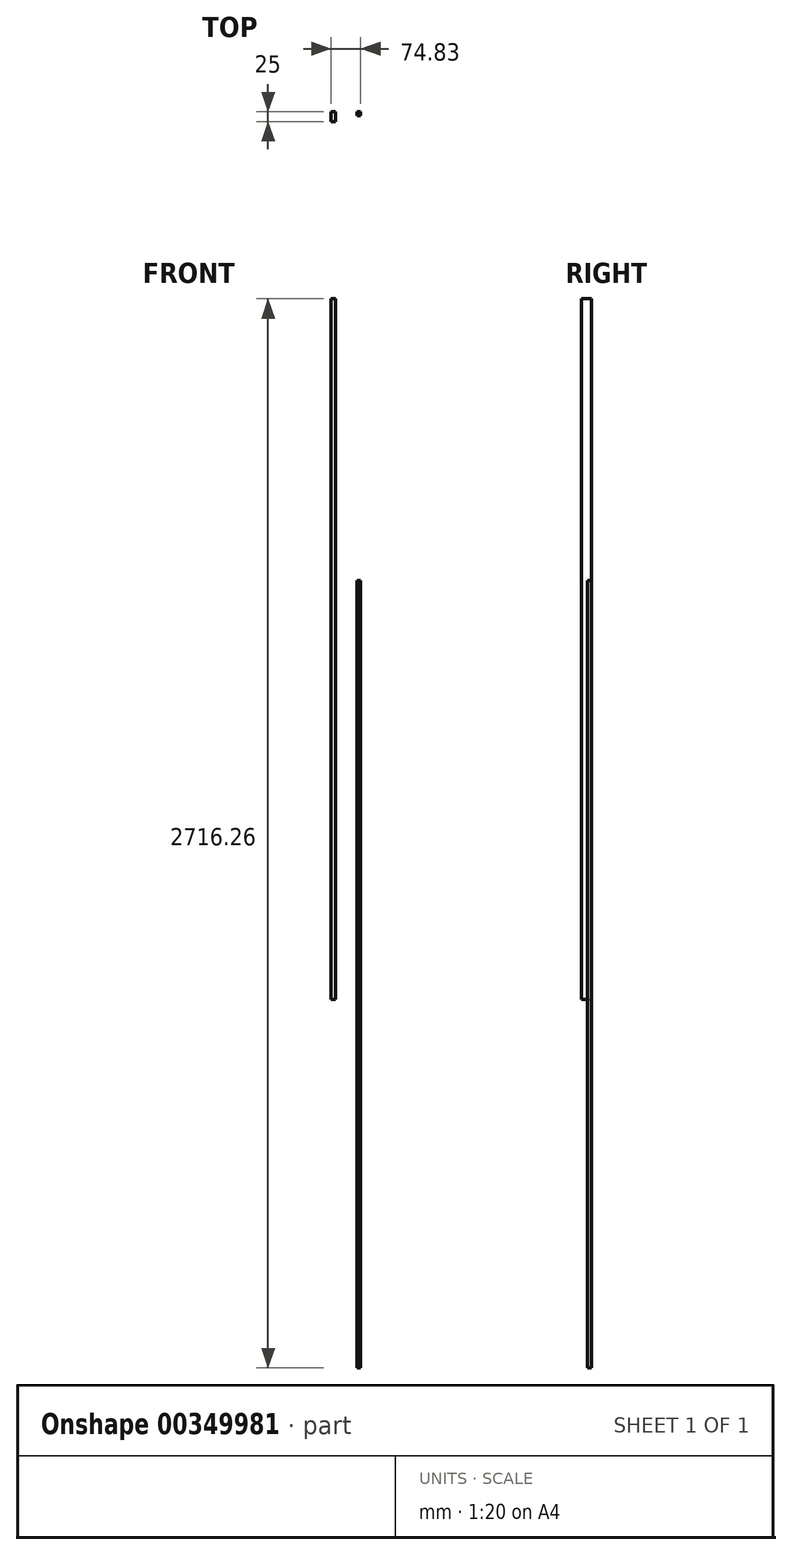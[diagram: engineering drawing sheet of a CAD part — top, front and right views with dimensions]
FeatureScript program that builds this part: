
annotation { "Feature Type Name" : "Feature", "Feature Type Description" : "" }
export const myFeature = defineFeature(function(context is Context, id is Id, definition is map)
    precondition{}
    {
        {
            var Q0;
            Q0=qCreatedBy(makeId("Front.planeOp"),FACE);
            var sketch = newSketch(context, id + "F0", { "sketchPlane" : qUnion([Q0])});
            skLineSegment(sketch, "E0.bottom", {"start": v(5, -1000) * mm, "end": v(-5, -1000) * mm});
            skLineSegment(sketch, "E0.top", {"start": v(5, 1000) * mm, "end": v(-5, 1000) * mm});
            skLineSegment(sketch, "E0.left", {"start": v(5, -1000) * mm, "end": v(5, 1000) * mm});
            skLineSegment(sketch, "E0.right", {"start": v(-5, -1000) * mm, "end": v(-5, 1000) * mm});
            skPoint(sketch, "E0.middle", {"position": v(0, 0) * mm});
            skSolve(sketch);
        }
        {
            var Q0;
            Q0 = qSketchRegion(id + "F0", true);
            extrude(context, id + "F1", {"entities" : qUnion([Q0]), "depth" : 10 * mm, "offsetDistance" : 25 * mm});
        }
        {
            var Q0;
            Q0=qCreatedBy(makeId("Front.planeOp"),FACE);
            var sketch = newSketch(context, id + "F2", { "sketchPlane" : qUnion([Q0])});
            skLineSegment(sketch, "E1.bottom", {"start": v(-69.83, 1716.26) * mm, "end": v(-58.97, 1716.26) * mm});
            skLineSegment(sketch, "E1.top", {"start": v(-69.83, -63.74) * mm, "end": v(-58.97, -63.74) * mm});
            skLineSegment(sketch, "E1.left", {"start": v(-69.83, 1716.26) * mm, "end": v(-69.83, -63.74) * mm});
            skLineSegment(sketch, "E1.right", {"start": v(-58.97, 1716.26) * mm, "end": v(-58.97, -63.74) * mm});
            skSolve(sketch);
        }
        {
            var Q0;
            Q0 = qSketchRegion(id + "F2", true);
            extrude(context, id + "F3", {"entities" : qUnion([Q0]), "depth" : 25 * mm, "offsetDistance" : 25 * mm});
        }
    });
